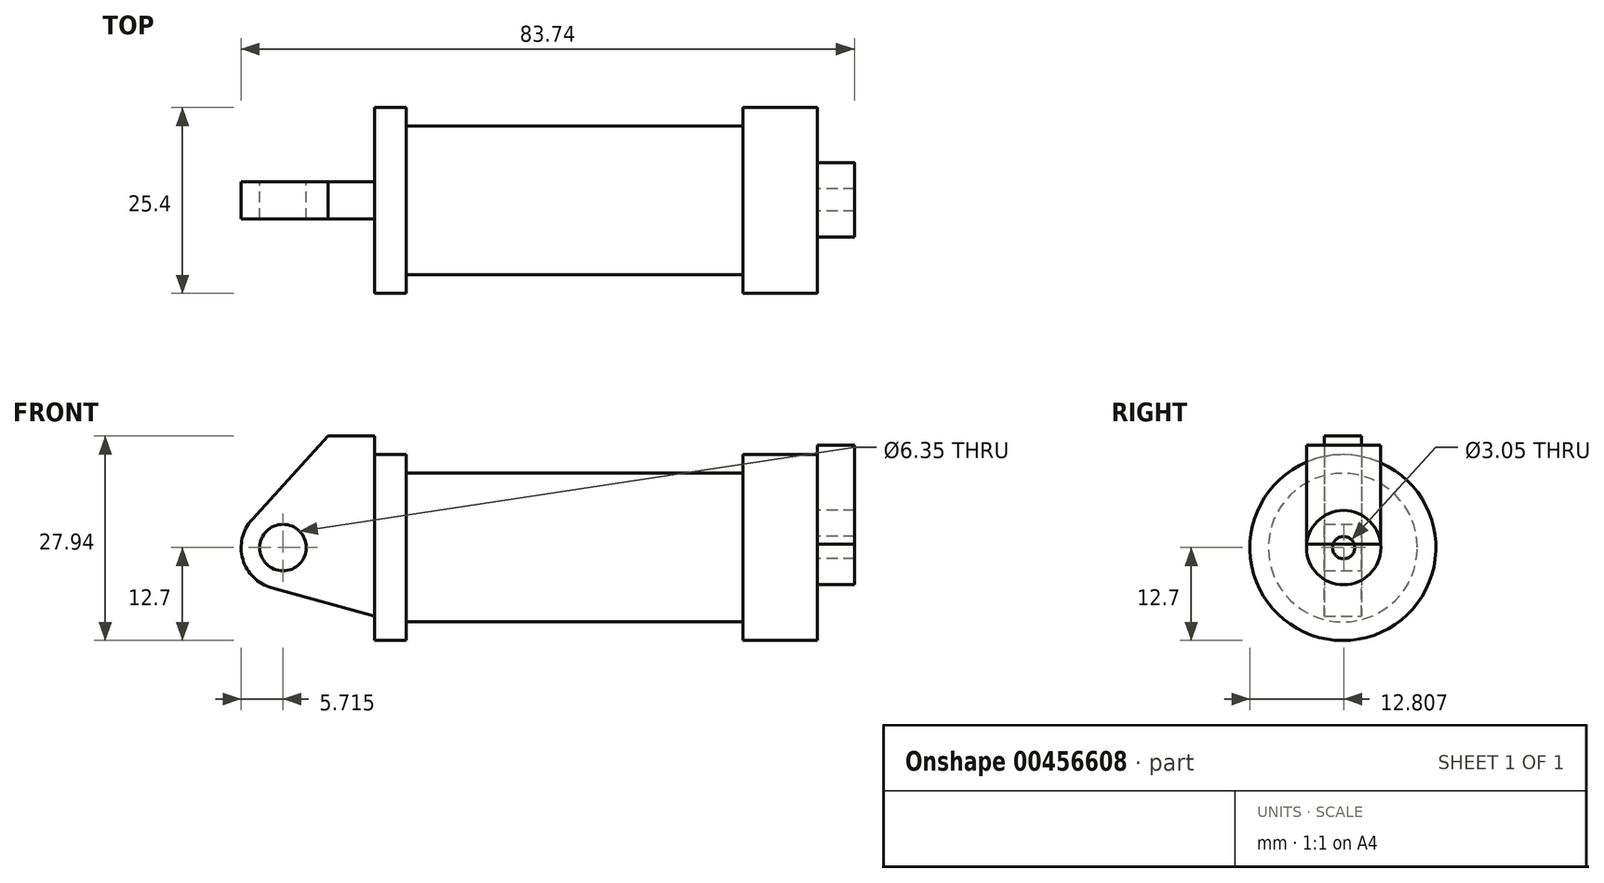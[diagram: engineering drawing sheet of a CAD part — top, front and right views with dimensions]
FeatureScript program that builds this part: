
annotation { "Feature Type Name" : "Feature", "Feature Type Description" : "" }
export const myFeature = defineFeature(function(context is Context, id is Id, definition is map)
    precondition{}
    {
        {
            var Q0;
            Q0=qCreatedBy(makeId("Front.planeOp"),FACE);
            var sketch = newSketch(context, id + "F0", { "sketchPlane" : qUnion([Q0])});
            skLineSegment(sketch, "E0", {"start": v(0, 0) * mm, "end": v(0, 12.7) * mm});
            skLineSegment(sketch, "E1", {"start": v(0, 12.7) * mm, "end": v(10.16, 12.7) * mm});
            skLineSegment(sketch, "E2", {"start": v(10.16, 12.7) * mm, "end": v(10.16, 10.16) * mm});
            skLineSegment(sketch, "E3", {"start": v(10.16, 10.16) * mm, "end": v(56.13, 10.16) * mm});
            skLineSegment(sketch, "E4", {"start": v(56.13, 10.16) * mm, "end": v(56.13, 12.7) * mm});
            skLineSegment(sketch, "E5", {"start": v(56.13, 12.7) * mm, "end": v(66.3, 12.7) * mm});
            skLineSegment(sketch, "E6", {"start": v(66.3, 12.7) * mm, "end": v(66.3, 0) * mm});
            skLineSegment(sketch, "E7", {"start": v(66.3, 0) * mm, "end": v(0, 0) * mm});
            skLineSegment(sketch, "E8", {"start": v(5.84, 15.24) * mm, "end": v(-0.5, 15.24) * mm});
            skLineSegment(sketch, "E9", {"start": v(-0.5, 15.24) * mm, "end": v(-10.88, 3.85) * mm});
            skLineSegment(sketch, "E10", {"start": v(0, 0) * mm, "end": v(-6.65, 0) * mm});
            skCircle(sketch, "E11", {"center": v(-6.65, 0) * mm, "radius": 5.72 * mm});
            skCircle(sketch, "E12", {"center": v(-6.65, 0) * mm, "radius": 3.18 * mm});
            skLineSegment(sketch, "E13", {"start": v(5.84, 15.24) * mm, "end": v(5.84, -9.4) * mm});
            skLineSegment(sketch, "E14", {"start": v(5.84, -9.4) * mm, "end": v(-8.18, -5.5) * mm});
            skSolve(sketch);
        }
        {
            var Q0;
            {var subQ0=sQuery(id+"F0.wireOp",EDGE,"E2");Q0=makeQuery(id+"F0.imprint","IMPRINT",FACE,{"disambiguationData":[TD([[makeQuery(id+"F0.imprint","IMPRINT",EDGE,{"derivedFrom":subQ0}),-1.0]])]});}
            var Q1;
            Q1=sQuery(id+"F0.wireOp",EDGE,"E7");
            revolve(context, id + "F1", {"entities" : qUnion([Q0]), "axis" : qUnion([Q1]), "revolveType" : RevolveType.FULL});
        }
        {
            var Q0;
            Q0=makeQuery(id+"F1.opRevolve","SWEPT_FACE",FACE,{"disambiguationData":[OSD([sQuery(id+"F0.wireOp",EDGE,"E6")])]});
            var sketch = newSketch(context, id + "F2", { "sketchPlane" : qUnion([Q0])});
            skSolve(sketch);
        }
        {
            var Q0;
            Q0=makeQuery(id+"F2.imprint","IMPRINT",FACE,{"disambiguationData":[TD([[makeQuery(id+"F2.imprint","IMPRINT",EDGE,{"derivedFrom":makeQuery(id+"F1.opRevolve","SWEPT_EDGE",EDGE,{"disambiguationData":[OSD([sQuery(id+"F0.wireOp",EDGE,"E5"),sQuery(id+"F0.wireOp",EDGE,"E6")])]})}),1.0]])]});
            var sketch = newSketch(context, id + "F3", { "sketchPlane" : qUnion([Q0])});
            skCircle(sketch, "E15", {"center": v(0.1, 0) * mm, "radius": 1.52 * mm});
            skCircle(sketch, "E16", {"center": v(0.1, 0) * mm, "radius": 5.08 * mm});
            skSolve(sketch);
        }
        {
            var Q0;
            Q0=makeQuery(id+"F2.imprint","IMPRINT",FACE,{"disambiguationData":[TD([[makeQuery(id+"F2.imprint","IMPRINT",EDGE,{"derivedFrom":makeQuery(id+"F1.opRevolve","SWEPT_EDGE",EDGE,{"disambiguationData":[OSD([sQuery(id+"F0.wireOp",EDGE,"E5"),sQuery(id+"F0.wireOp",EDGE,"E6")])]})}),1.0]])]});
            var sketch = newSketch(context, id + "F4", { "sketchPlane" : qUnion([Q0])});
            skLineSegment(sketch, "E17.bottom", {"start": v(-4.98, 0.47) * mm, "end": v(5.17, 0.47) * mm});
            skLineSegment(sketch, "E17.top", {"start": v(-4.98, 14) * mm, "end": v(5.17, 14) * mm});
            skLineSegment(sketch, "E17.left", {"start": v(-4.98, 0.47) * mm, "end": v(-4.98, 14) * mm});
            skLineSegment(sketch, "E17.right", {"start": v(5.17, 0.47) * mm, "end": v(5.17, 14) * mm});
            skSolve(sketch);
        }
        {
            var Q0;
            {var subQ0=sQuery(id+"F4.wireOp",EDGE,"E17.bottom");Q0=makeQuery(id+"F4.imprint","IMPRINT",FACE,{"disambiguationData":[TD([[makeQuery(id+"F4.imprint","IMPRINT",EDGE,{"derivedFrom":subQ0}),1.0]])]});}
            var Q1;
            {var subQ0=sQuery(id+"F4.wireOp",EDGE,"E17.top");Q1=makeQuery(id+"F4.imprint","IMPRINT",FACE,{"disambiguationData":[TD([[makeQuery(id+"F4.imprint","IMPRINT",EDGE,{"derivedFrom":subQ0}),-1.0]])]});}
            extrude(context, id + "F5", {"entities" : qUnion([Q0, Q1]), "operationType" : NewBodyOperationType.ADD, "depth" : 5.08 * mm});
        }
        {
            var Q0;
            Q0=makeQuery(id+"F3.imprint","IMPRINT",FACE,{"disambiguationData":[TD([[makeQuery(id+"F3.imprint","IMPRINT",EDGE,{"derivedFrom":sQuery(id+"F3.wireOp",EDGE,"E15")}),-1.0]])]});
            var Q1;
            Q1=sQuery(id+"F3.wireOp",EDGE,"E16");
            extrude(context, id + "F6", {"entities" : qUnion([Q0]), "surfaceEntities" : qUnion([Q1]), "depth" : 5.08 * mm});
        }
        {
            var Q0;
            {var subQ1=sQuery(id+"F0.wireOp",EDGE,"E0");Q0=makeQuery(id+"F0.imprint","IMPRINT",FACE,{"disambiguationData":[TD([[makeQuery(id+"F0.imprint","IMPRINT",EDGE,{"derivedFrom":subQ1}),1.0]])]});}
            var Q1;
            {var subQ0=sQuery(id+"F0.wireOp",EDGE,"E0");Q1=makeQuery(id+"F0.imprint","IMPRINT",FACE,{"disambiguationData":[TD([[makeQuery(id+"F0.imprint","IMPRINT",EDGE,{"derivedFrom":subQ0}),-1.0]])]});}
            var Q2;
            {var subQ0=sQuery(id+"F0.wireOp",EDGE,"E14");Q2=makeQuery(id+"F0.imprint","IMPRINT",FACE,{"disambiguationData":[TD([[makeQuery(id+"F0.imprint","IMPRINT",EDGE,{"derivedFrom":subQ0}),-1.0]])]});}
            var Q3;
            {var subQ5=sQuery(id+"F0.wireOp",EDGE,"E12");Q3=makeQuery(id+"F0.imprint","IMPRINT",FACE,{"disambiguationData":[TD([[makeQuery(id+"F0.imprint","IMPRINT",EDGE,{"derivedFrom":subQ5}),-1.0]])]});}
            extrude(context, id + "F7", {"entities" : qUnion([Q0, Q1, Q2, Q3]), "operationType" : NewBodyOperationType.ADD, "endBound" : BoundingType.SYMMETRIC, "depth" : 5.08 * mm});
        }
    });
